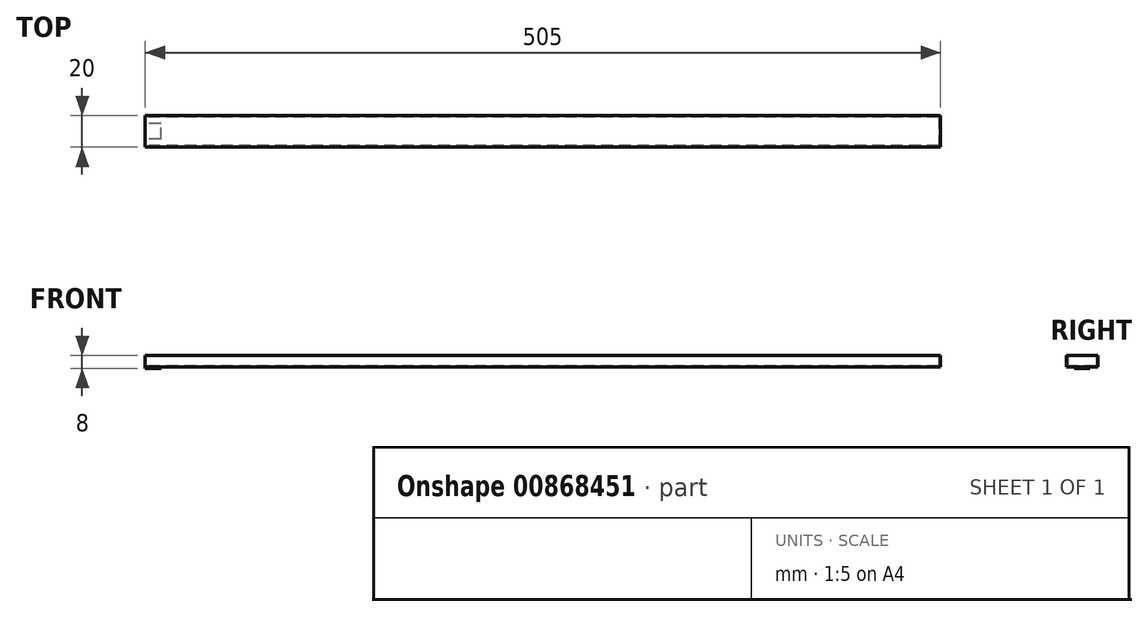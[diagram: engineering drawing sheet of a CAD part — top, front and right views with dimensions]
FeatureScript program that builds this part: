
annotation { "Feature Type Name" : "Feature", "Feature Type Description" : "" }
export const myFeature = defineFeature(function(context is Context, id is Id, definition is map)
    precondition{}
    {
        {
            var Q0;
            Q0=qCreatedBy(makeId("Top.planeOp"),FACE);
            var sketch = newSketch(context, id + "F0", { "sketchPlane" : qUnion([Q0])});
            skLineSegment(sketch, "E0.bottom", {"start": v(-168.14, -249.84) * mm, "end": v(336.86, -249.84) * mm});
            skLineSegment(sketch, "E0.top", {"start": v(-168.14, -269.84) * mm, "end": v(336.86, -269.84) * mm});
            skLineSegment(sketch, "E0.left", {"start": v(-168.14, -249.84) * mm, "end": v(-168.14, -269.84) * mm});
            skLineSegment(sketch, "E0.right", {"start": v(336.86, -249.84) * mm, "end": v(336.86, -269.84) * mm});
            skLineSegment(sketch, "E1.bottom", {"start": v(-158.14, -264.84) * mm, "end": v(-168.14, -264.84) * mm});
            skLineSegment(sketch, "E1.top", {"start": v(-158.14, -254.84) * mm, "end": v(-168.14, -254.84) * mm});
            skLineSegment(sketch, "E1.left", {"start": v(-158.14, -264.84) * mm, "end": v(-158.14, -254.84) * mm});
            skLineSegment(sketch, "E1.right", {"start": v(-168.14, -264.84) * mm, "end": v(-168.14, -254.84) * mm});
            skPoint(sketch, "E1.middle", {"position": v(-163.14, -259.84) * mm});
            skSolve(sketch);
        }
        {
            var Q0;
            {var subQ3=sQuery(id+"F0.wireOp",EDGE,"E0.bottom");Q0=makeQuery(id+"F0.imprint","IMPRINT",FACE,{"disambiguationData":[TD([[makeQuery(id+"F0.imprint","IMPRINT",EDGE,{"derivedFrom":subQ3}),-1.0]])]});}
            var Q1;
            Q1=makeQuery(id+"F0.imprint","IMPRINT",FACE,{"disambiguationData":[TD([[makeQuery(id+"F0.imprint","IMPRINT",EDGE,{"derivedFrom":sQuery(id+"F0.wireOp",EDGE,"E1.bottom")}),-1.0]])]});
            extrude(context, id + "F1", {"entities" : qUnion([Q0, Q1]), "depth" : 7 * mm, "offsetDistance" : 25 * mm});
        }
        {
            var Q0;
            Q0=makeQuery(id+"F0.imprint","IMPRINT",FACE,{"disambiguationData":[TD([[makeQuery(id+"F0.imprint","IMPRINT",EDGE,{"derivedFrom":sQuery(id+"F0.wireOp",EDGE,"E1.bottom")}),-1.0]])]});
            extrude(context, id + "F2", {"entities" : qUnion([Q0]), "operationType" : NewBodyOperationType.ADD, "oppositeDirection" : true, "depth" : 1 * mm, "offsetDistance" : 25 * mm});
        }
        {
            var Q0;
            {var subQ0=sQuery(id+"F0.wireOp",EDGE,"E1.right");Q0=makeQuery(id+"F2.boolean.opBoolean","MERGE",FACE,{"derivedFrom":[makeQuery(id+"F1.opExtrude","SWEPT_FACE",FACE,{"disambiguationData":[OSD([sQuery(id+"F0.wireOp",EDGE,"E0.left"),subQ0])]}),makeQuery(id+"F2.opExtrude","SWEPT_FACE",FACE,{"disambiguationData":[OSD([subQ0])]})]});}
            var sketch = newSketch(context, id + "F3", { "sketchPlane" : qUnion([Q0])});
            skLineSegment(sketch, "E2.bottom", {"start": v(250.84, 6.5) * mm, "end": v(268.84, 6.5) * mm});
            skLineSegment(sketch, "E2.top", {"start": v(250.84, 0.5) * mm, "end": v(268.84, 0.5) * mm});
            skLineSegment(sketch, "E2.left", {"start": v(250.84, 6.5) * mm, "end": v(250.84, 0.5) * mm});
            skLineSegment(sketch, "E2.right", {"start": v(268.84, 6.5) * mm, "end": v(268.84, 0.5) * mm});
            skPoint(sketch, "E2.middle", {"position": v(259.84, 3.5) * mm});
            skSolve(sketch);
        }
        {
            var Q0;
            Q0=makeQuery(id+"F3.imprint","IMPRINT",FACE,{"disambiguationData":[TD([[makeQuery(id+"F3.imprint","IMPRINT",EDGE,{"derivedFrom":sQuery(id+"F3.wireOp",EDGE,"E2.bottom")}),-1.0]])]});
            extrude(context, id + "F4", {"entities" : qUnion([Q0]), "operationType" : NewBodyOperationType.REMOVE, "oppositeDirection" : true, "depth" : 504 * mm, "offsetDistance" : 25 * mm});
        }
    });
